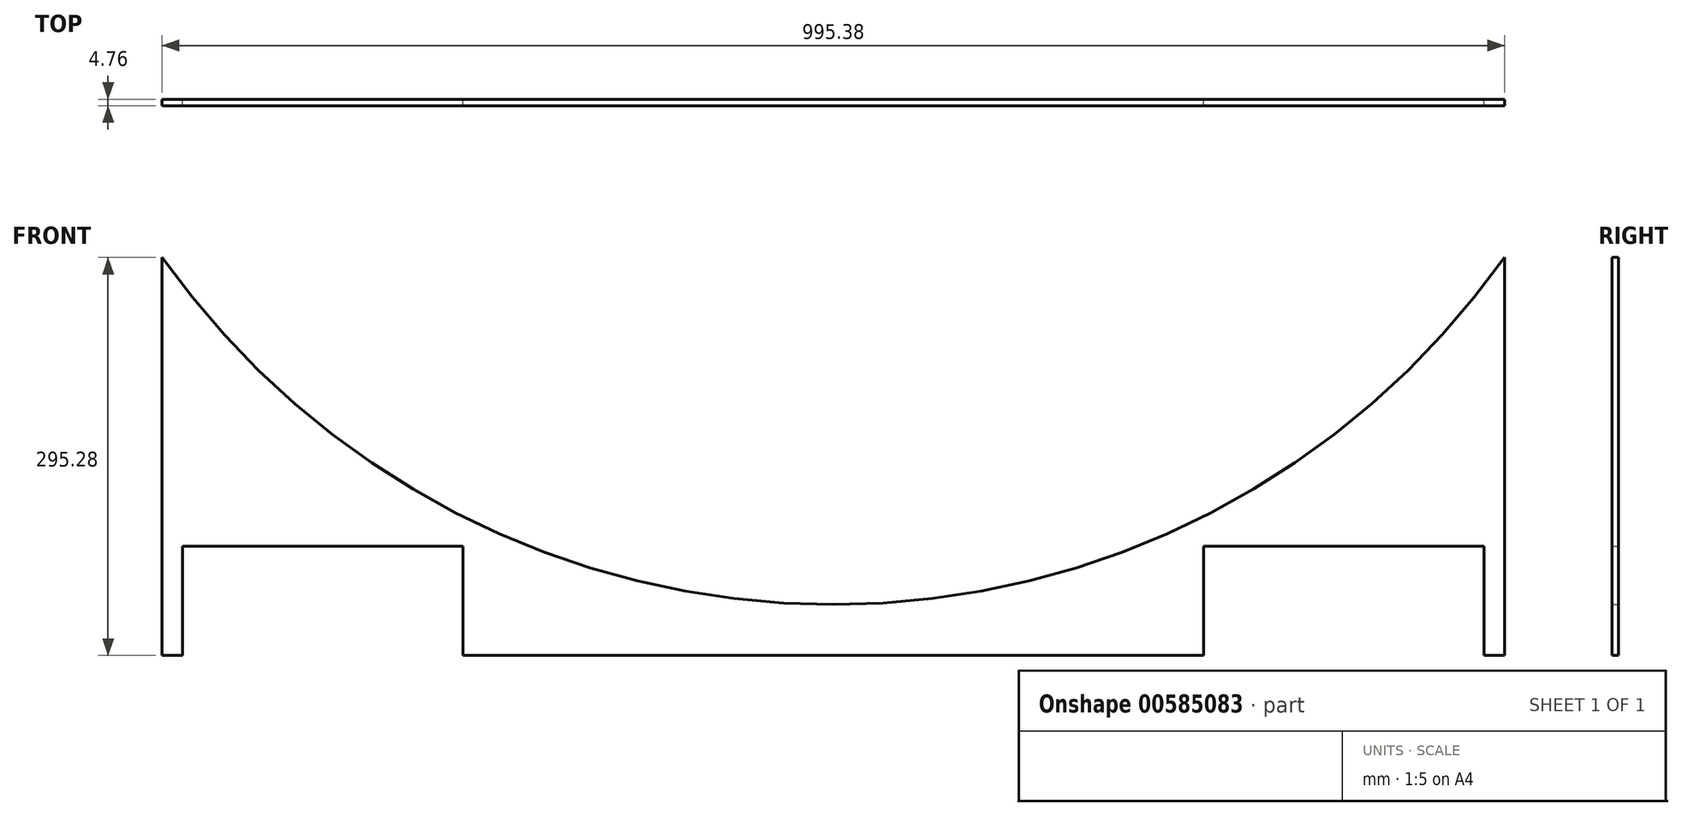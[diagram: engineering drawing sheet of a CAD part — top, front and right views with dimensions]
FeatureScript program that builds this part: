
annotation { "Feature Type Name" : "Feature", "Feature Type Description" : "" }
export const myFeature = defineFeature(function(context is Context, id is Id, definition is map)
    precondition{}
    {
        {
            var Q0;
            Q0=qCreatedBy(makeId("Front.planeOp"),FACE);
            var sketch = newSketch(context, id + "F0", { "sketchPlane" : qUnion([Q0])});
            skLineSegment(sketch, "E0", {"start": v(0, 0) * mm, "end": v(15.09, 0) * mm});
            skLineSegment(sketch, "E1", {"start": v(15.09, 0) * mm, "end": v(15.09, 80.96) * mm});
            skLineSegment(sketch, "E2", {"start": v(15.09, 80.96) * mm, "end": v(223.05, 80.96) * mm});
            skLineSegment(sketch, "E3", {"start": v(223.05, 80.96) * mm, "end": v(223.05, 0) * mm});
            skLineSegment(sketch, "E4", {"start": v(223.05, 0) * mm, "end": v(772.33, 0) * mm});
            skLineSegment(sketch, "E5", {"start": v(772.33, 0) * mm, "end": v(772.33, 80.96) * mm});
            skLineSegment(sketch, "E6", {"start": v(772.33, 80.96) * mm, "end": v(980.29, 80.96) * mm});
            skLineSegment(sketch, "E7", {"start": v(980.29, 80.96) * mm, "end": v(980.29, 0) * mm});
            skLineSegment(sketch, "E8", {"start": v(980.29, 0) * mm, "end": v(995.38, 0) * mm});
            skLineSegment(sketch, "E9", {"start": v(995.38, 0) * mm, "end": v(995.38, 295.27) * mm});
            skLineSegment(sketch, "E10", {"start": v(0, 0) * mm, "end": v(0, 295.28) * mm});
            skArc(sketch, "E11", {"start": v(0, 295.27) * mm, "mid": v(497.69, 37.7) * mm, "end": v(995.38, 295.27) * mm});
            skLineSegment(sketch, "E12", {"start": v(497.69, 0) * mm, "end": v(497.69, -107.93) * mm, "construction": true});
            skSolve(sketch);
        }
        {
            var Q0;
            Q0=makeQuery(id+"F0.imprint","IMPRINT",FACE,{"disambiguationData":[TD([[makeQuery(id+"F0.imprint","IMPRINT",EDGE,{"derivedFrom":sQuery(id+"F0.wireOp",EDGE,"E0")}),1.0]])]});
            extrude(context, id + "F1", {"entities" : qUnion([Q0]), "depth" : 4.76 * mm, "offsetDistance" : 25.4 * mm});
        }
    });
